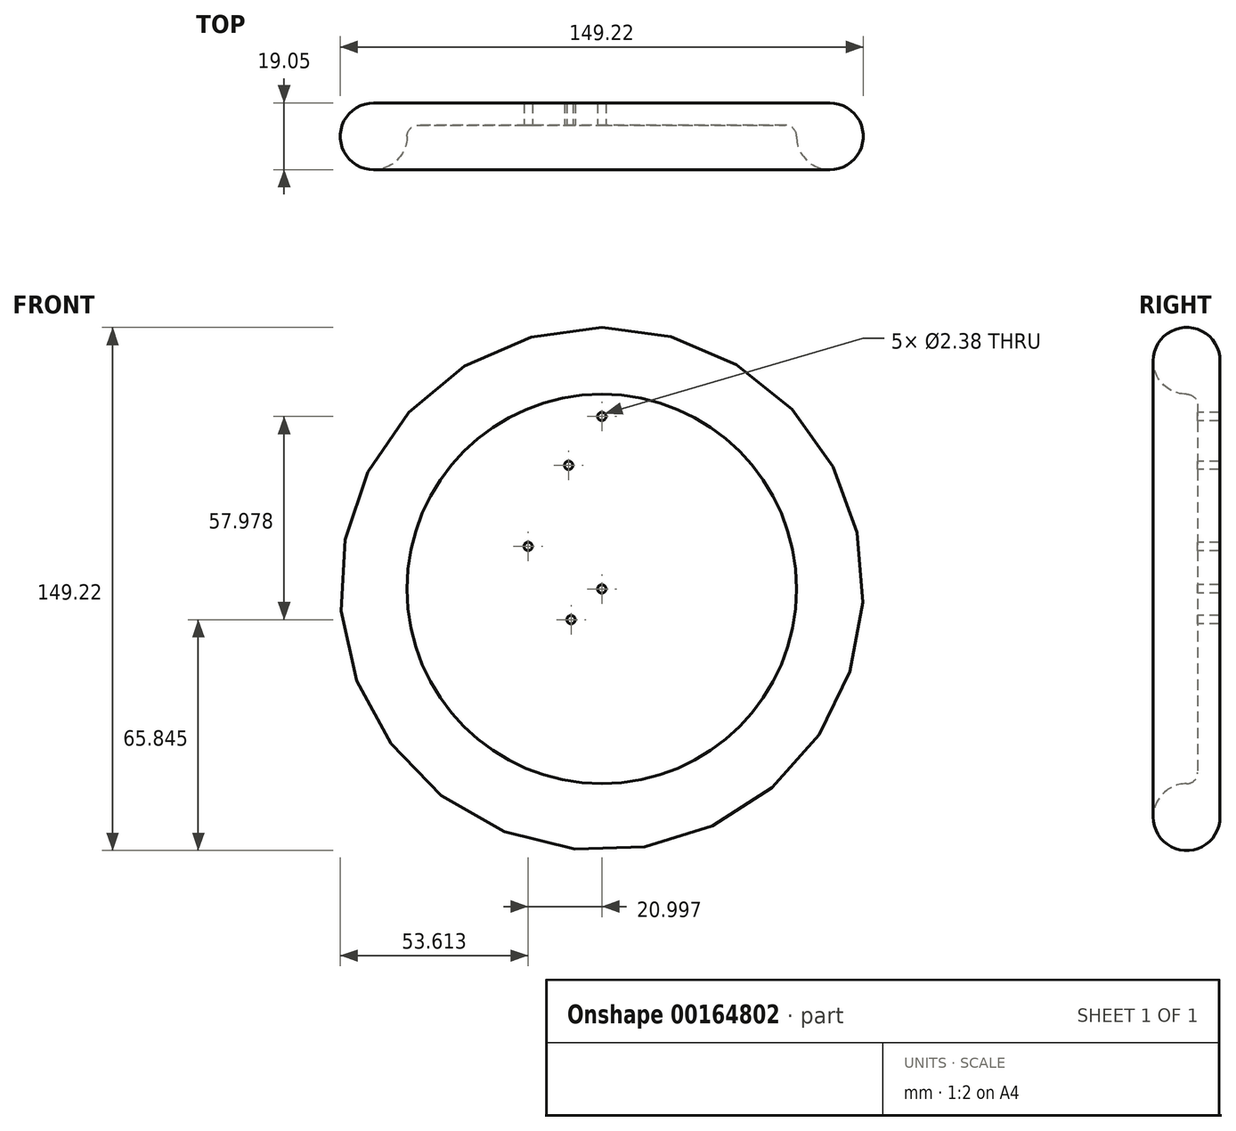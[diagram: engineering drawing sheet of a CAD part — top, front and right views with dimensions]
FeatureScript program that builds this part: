
annotation { "Feature Type Name" : "Feature", "Feature Type Description" : "" }
export const myFeature = defineFeature(function(context is Context, id is Id, definition is map)
    precondition{}
    {
        {
            var Q0;
            Q0=qCreatedBy(makeId("Top.planeOp"),FACE);
            var sketch = newSketch(context, id + "F0", { "sketchPlane" : qUnion([Q0])});
            skLineSegment(sketch, "E0", {"start": v(0, 0) * mm, "end": v(65.09, 0) * mm});
            skArc(sketch, "E1", {"start": v(55.56, -9.53) * mm, "mid": v(71.82, -16.26) * mm, "end": v(65.09, 0) * mm});
            skLineSegment(sketch, "E2", {"start": v(0, 0) * mm, "end": v(0, -6.35) * mm});
            skLineSegment(sketch, "E3.bottom", {"start": v(0, -6.35) * mm, "end": v(52.39, -6.35) * mm});
            skArc(sketch, "E4", {"start": v(55.56, -9.52) * mm, "mid": v(54.63, -7.28) * mm, "end": v(52.39, -6.35) * mm});
            skLineSegment(sketch, "E5", {"start": v(65.09, -9.52) * mm, "end": v(65.09, -6.35) * mm, "construction": true});
            skLineSegment(sketch, "E6", {"start": v(65.09, -6.35) * mm, "end": v(52.39, -6.35) * mm, "construction": true});
            skSolve(sketch);
        }
        {
            var Q0;
            Q0=qCreatedBy(makeId("Front.planeOp"),FACE);
            var sketch = newSketch(context, id + "F1", { "sketchPlane" : qUnion([Q0])});
            skCircle(sketch, "E7", {"center": v(0, 0) * mm, "radius": 12.7 * mm});
            skSolve(sketch);
        }
        {
            var Q0;
            Q0=makeQuery(id+"F0.imprint","IMPRINT",FACE,{"disambiguationData":[TD([[makeQuery(id+"F0.imprint","IMPRINT",EDGE,{"derivedFrom":sQuery(id+"F0.wireOp",EDGE,"E0")}),-1.0]])]});
            var Q1;
            Q1=sQuery(id+"F1.wireOp",EDGE,"E7");
            revolve(context, id + "F2", {"entities" : qUnion([Q0]), "axis" : qUnion([Q1]), "revolveType" : RevolveType.FULL});
        }
        {
            var Q0;
            Q0=makeQuery(id+"F2.opRevolve","SWEPT_FACE",FACE,{"disambiguationData":[OSD([sQuery(id+"F0.wireOp",EDGE,"E3.bottom")])]});
            var sketch = newSketch(context, id + "F3", { "sketchPlane" : qUnion([Q0])});
            skLineSegment(sketch, "E8", {"start": v(0, 0) * mm, "end": v(0, 49.21) * mm, "construction": true});
            skCircle(sketch, "E9", {"center": v(0, 49.21) * mm, "radius": 3.18 * mm, "construction": true});
            skCircle(sketch, "E10", {"center": v(0, 49.21) * mm, "radius": 1.2 * mm});
            skSolve(sketch);
        }
        {
            var Q0;
            Q0 = qSketchRegion(id + "F3", true);
            var Q1;
            Q1=makeQuery(id+"F2.opRevolve","SWEPT_FACE",FACE,{"disambiguationData":[OSD([sQuery(id+"F0.wireOp",EDGE,"E0")])]});
            extrude(context, id + "F4", {"entities" : qUnion([Q0]), "operationType" : NewBodyOperationType.REMOVE, "endBound" : BoundingType.UP_TO_SURFACE, "oppositeDirection" : true, "endBoundEntityFace" : qUnion([Q1]), "depth" : 25.4 * mm});
        }
        {
            var Q0;
            Q0=makeQuery(id+"F2.opRevolve","SWEPT_FACE",FACE,{"disambiguationData":[OSD([sQuery(id+"F0.wireOp",EDGE,"E3.bottom")])]});
            var sketch = newSketch(context, id + "F5", { "sketchPlane" : qUnion([Q0])});
            skLineSegment(sketch, "E11", {"start": v(0, 0) * mm, "end": v(-9.45, 35.27) * mm, "construction": true});
            skLineSegment(sketch, "E12", {"start": v(-9.45, 35.27) * mm, "end": v(-12.3, 45.92) * mm, "construction": true});
            skLineSegment(sketch, "E13", {"start": v(-24.6, 42.62) * mm, "end": v(0, 49.21) * mm, "construction": true});
            skCircle(sketch, "E14", {"center": v(-9.45, 35.27) * mm, "radius": 1.2 * mm});
            skArc(sketch, "E15", {"start": v(0, 49.21) * mm, "mid": v(-12.74, 47.54) * mm, "end": v(-24.6, 42.62) * mm, "construction": true});
            skSolve(sketch);
        }
        {
            var Q0;
            Q0 = qSketchRegion(id + "F5", true);
            var Q1;
            Q1=makeQuery(id+"F2.opRevolve","SWEPT_FACE",FACE,{"disambiguationData":[OSD([sQuery(id+"F0.wireOp",EDGE,"E0")])]});
            extrude(context, id + "F6", {"entities" : qUnion([Q0]), "operationType" : NewBodyOperationType.REMOVE, "endBound" : BoundingType.UP_TO_SURFACE, "oppositeDirection" : true, "endBoundEntityFace" : qUnion([Q1]), "depth" : 25.4 * mm});
        }
        {
            var Q0;
            Q0=makeQuery(id+"F2.opRevolve","SWEPT_FACE",FACE,{"disambiguationData":[OSD([sQuery(id+"F0.wireOp",EDGE,"E3.bottom")])]});
            var sketch = newSketch(context, id + "F7", { "sketchPlane" : qUnion([Q0])});
            skLineSegment(sketch, "E16", {"start": v(0, 0) * mm, "end": v(-21, 12.12) * mm, "construction": true});
            skLineSegment(sketch, "E17", {"start": v(-21, 12.12) * mm, "end": v(-30.54, 17.63) * mm, "construction": true});
            skLineSegment(sketch, "E18", {"start": v(-35.27, 9.45) * mm, "end": v(-25.82, 25.82) * mm, "construction": true});
            skCircle(sketch, "E19", {"center": v(-21, 12.12) * mm, "radius": 1.2 * mm});
            skSolve(sketch);
        }
        {
            var Q0;
            Q0 = qSketchRegion(id + "F7", true);
            var Q1;
            Q1=makeQuery(id+"F2.opRevolve","SWEPT_FACE",FACE,{"disambiguationData":[OSD([sQuery(id+"F0.wireOp",EDGE,"E0")])]});
            extrude(context, id + "F8", {"entities" : qUnion([Q0]), "operationType" : NewBodyOperationType.REMOVE, "endBound" : BoundingType.UP_TO_SURFACE, "oppositeDirection" : true, "endBoundEntityFace" : qUnion([Q1]), "depth" : 25.4 * mm});
        }
        {
            var Q0;
            Q0=makeQuery(id+"F2.opRevolve","SWEPT_FACE",FACE,{"disambiguationData":[OSD([sQuery(id+"F0.wireOp",EDGE,"E3.bottom")])]});
            var sketch = newSketch(context, id + "F9", { "sketchPlane" : qUnion([Q0])});
            skLineSegment(sketch, "E20", {"start": v(-21, -12.12) * mm, "end": v(-12.12, -21) * mm, "construction": true});
            skLineSegment(sketch, "E21", {"start": v(-16.56, -16.56) * mm, "end": v(-8.77, -8.77) * mm, "construction": true});
            skCircle(sketch, "E22", {"center": v(-8.77, -8.77) * mm, "radius": 1.2 * mm});
            skCircle(sketch, "E23", {"center": v(0, 0) * mm, "radius": 1.2 * mm});
            skSolve(sketch);
        }
        {
            var Q0;
            Q0 = qSketchRegion(id + "F9", true);
            var Q1;
            Q1=makeQuery(id+"F2.opRevolve","SWEPT_FACE",FACE,{"disambiguationData":[OSD([sQuery(id+"F0.wireOp",EDGE,"E0")])]});
            extrude(context, id + "F10", {"entities" : qUnion([Q0]), "operationType" : NewBodyOperationType.REMOVE, "endBound" : BoundingType.UP_TO_SURFACE, "oppositeDirection" : true, "endBoundEntityFace" : qUnion([Q1]), "depth" : 25.4 * mm});
        }
    });
